# Revit family: Shower-Showerhead-KOHLER-Awaken-K-72418
name_source: partatom
category: Plumbing Fixtures
revit_build: Autodesk Revit 2015 (Build: 20140606_1530(x64)
units: mm (PartAtom-declared; Revit-internal decimal feet)

## types (2) — shared parameters
ADA Compliant = No
Assembly Code = D2010700
CW Connection = No
Date Modified = 10/06/2017
Default Elevation = 42"
Description = Awaken G90 2.0 gpm multifunction showerhead
Flow Rate = 2 GPM
HW Connection = Yes
Height = 3 13/16"
Inlet Connector = Inlet Connection
Length = 2 3/4"
Manufacturer = KOHLER Co.
MasterFormat 1995 = 15410
MasterFormat 2004 = 22.41.23
Material = Premium Metal Construction
Outlet Connector = Outlet Connection
Pressure = 0.00 psi
Product Documentation Link = http://www.us.kohler.com
Product Name = Awaken
Product Page URL = http://www.us.kohler.com
URL = https://www.us.kohler.com
Vent Connection = No
Waste Connection = No
Width = 3 9/16"

## per-type parameters (varying)
| type | Finish | Model | Type |
| CP-Polished Chrome | Kohler-Metal-CP-Polished_Chrome | K-72418-CP | 1 |
| BN-Vibrant Brushed Nickel | Kohler-Metal-BN-Vibrant_Brushed_Nickel | K-72418-BN | 2 |

## geometry (parser evidence)
native form markers: Sweep x5
no freeform markers — native parametric forms only
